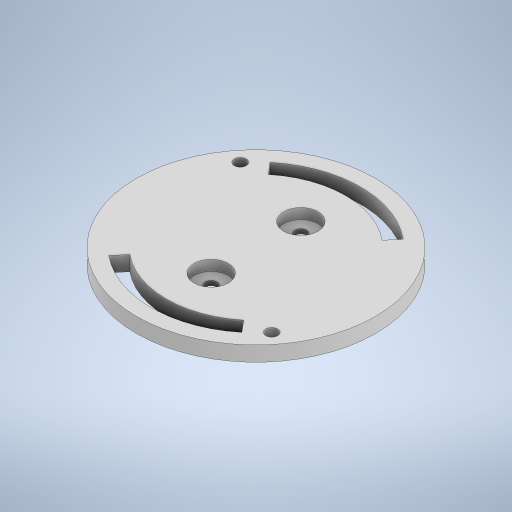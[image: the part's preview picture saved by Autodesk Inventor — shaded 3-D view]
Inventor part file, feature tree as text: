
AUTODESK INVENTOR PART (.ipt)
format: ipt  version: 2023 (Build 270158000, 158)  size: 317,952 bytes
history: native  units: in
note: dims shown in document units (in); Inventor stores cm internally (conversion verified against a paired STEP export)
features: extrude x6, sketch x5, plane x1, mirror x1, projected_geometry x1
ambient origin geometry x8: Origin, YZ Plane, XZ Plane, XY Plane, X Axis, Y Axis, Z Axis, Center Point
bodies: Solid1 (feature_tree)
feature tree (14):
  extrude  "Extrusion1"  Depth=0.1969in TaperAngle=0.0deg
  extrude  "Extrusion5"  Depth=0.9843in
  extrude  "Extrusion7"  Depth=0.9843in
  plane  "Work Plane1"
  mirror  "Mirror1"
  extrude  "Extrusion8"  Depth=0.7874in
  extrude  "Extrusion9"  Depth=0.1969in
  extrude  "Extrusion10"  TaperAngle=120.0deg  [1 undecoded]
  sketch  "Sketch1"  dims[d0=3.1496in d1=0.1969in d2=0.0in]
  sketch  "Sketch8"  dims[d19=0.9843in d20=0.7874in]
  sketch  "Sketch9"  dims[d22=0.1575in d23=0.0in d46=0.9843in]
  projected_geometry  "Projected Loop1"
  sketch  "Sketch10"  dims[d47=180.0deg d48=0.7874in]
  sketch  "Sketch11"  dims[d53=0.1969in d54=0.1969in d55=120.0deg d56=0.3937in d57=0.0in d58=0.1181in d60=0.8933in d61=0.5906in d62=0.4528in d63=0.5906in d64=0.4528in d65=0.1378in d66=0.0in d68=0.1575in d69=0.1575in d70=0.1181in d71=0.0in d72=0.1969in d73=0.1969in d74=0.1575in d75=0.1969in d76=0.1969in d77=0.1575in d78=0.3937in d79=0.0in d10=0.0197in d11=0.0344in d12=0.0197in d13=0.0344in d59=0.0344in]
note: 1 required parameter value undecoded (feature->parameter linkage not recoverable at this tier; creation-order binding heuristic only, values carry confidence <= 0.55)
